FCSTD DOCUMENT  (FreeCAD 0.20R29177 (Git))
Label: Frame_Shape_T
License: All rights reserved
LicenseURL: http://en.wikipedia.org/wiki/All_rights_reserved
objects: App::Link×4, Spreadsheet::Sheet×1, App::Part×1
EXTERNAL_REF file=Frame_Bracket_End_OneHole.FCStd obj=PocketBody
EXTERNAL_REF file=Frame_Bracket_End_TwoHole.FCStd obj=PadBody
EXTERNAL_REF file=../../Master_of_Puppets.FCStd obj=Alternator
EXTERNAL_REF file=../../Master_of_Puppets.FCStd obj=Spreadsheet
EXTERNAL_REF file=../../Master_of_Puppets.FCStd obj=WindTurbine
EXTERNAL_REF file=../../YawBearing/YawBearing_Plate_Bottom.FCStd obj=PocketBody
EXTERNAL_REF file=Frame_Channel.FCStd obj=Body

FEATURE [App::Link] Link001  label="Bracket_End_OneHole"
  LinkPlacement = pos=(0,0,0) rot=(0,1,0;3.14159rad)
  LinkTransform = true
  LinkedObject = -> <external Frame_Bracket_End_OneHole.FCStd>#PocketBody
  Placement = pos=(0,0,0) rot=(0,1,0;3.14159rad)
FEATURE [App::Link] Link002  label="Bracket_End_TwoHole"
  LinkPlacement = pos=(0,0,237.25) rot=(0,1,0;3.14159rad)
  LinkTransform = true
  LinkedObject = -> <external Frame_Bracket_End_TwoHole.FCStd>#PadBody
  Placement = pos=(0,0,237.25) rot=(0,1,0;3.14159rad)
  expr: .LinkPlacement.Base.z = Spreadsheet.ChannelSectionHeight
FEATURE [Spreadsheet::Sheet] Spreadsheet
  cells = A1=Inputs; A2=ChannelSectionHeight; B2(ChannelSectionHeight)==Master_of_Puppets#Alternator.BC; A3=MetalLengthL; B3(MetalLengthL)==Master_of_Puppets#Spreadsheet.MetalLengthL; A4=MetalThicknessL; B4(MetalThicknessL)==Master_of_Puppets#Spreadsheet.MetalThicknessL; A5=SmallVerticalDistanceFromCenter; B5(SmallVerticalDistanceFromCenter)==Master_of_Puppets#WindTurbine.SmallVerticalDistanceFromCenter; A6=Calculated; A7=BottomPlateX; B7(BottomPlateX)==-SmallVerticalDistanceFromCenter; A8=BottomPlateY; B8(BottomPlateY)==MetalLengthL - MetalThicknessL; A9=BottomPlateZ; B9(BottomPlateZ)==ChannelSectionHeight + MetalThicknessL
FEATURE [App::Link] Link003  label="Plate_Bottom"
  LinkPlacement = pos=(-147.5,44,243.25) rot=(0.707107,0,0.707107;3.14159rad)
  LinkedObject = -> <external ../../YawBearing/YawBearing_Plate_Bottom.FCStd>#PocketBody
  Placement = pos=(-147.5,44,243.25) rot=(0.707107,0,0.707107;3.14159rad)
  expr: .Placement.Base.x = Spreadsheet.BottomPlateX
  expr: .Placement.Base.y = Spreadsheet.BottomPlateY
  expr: .Placement.Base.z = Spreadsheet.BottomPlateZ
FEATURE [App::Link] Link004  label="Channel"
  LinkTransform = true
  LinkedObject = -> <external Frame_Channel.FCStd>#Body
FEATURE [App::Part] Part  label="Frame_Shape_T"
  Group = -> [Link004,Link001,Link002,Link003]
  Origin = -> Origin

RESOLVED EXTERNAL PARTS (link-assembly join: the EXTERNAL_REF files above that resolve inside this repo's crawl, each included once):
---- part ../../Master_of_Puppets.FCStd = doc fcstd_6404554055c4 (61625 chars; too large to inline — full recipe in that document) ----
---- part ../../YawBearing/YawBearing_Plate_Bottom.FCStd = doc fcstd_9afb94730c02 ----
FCSTD DOCUMENT  (FreeCAD 0.21R33675 (Git))
Label: YawBearing_Plate_Bottom
License: All rights reserved
LicenseURL: http://en.wikipedia.org/wiki/All_rights_reserved
objects: Sketcher::SketchObject×2, PartDesign::Pad×1, PartDesign::Pocket×1, Spreadsheet::Sheet×1, PartDesign::Body×1
note: 7 computed .brp shape members not serialized (recipe doc carries the construction recipe); baked Part::Feature solids carry a one-line shape summary decoded from their .brp
EXTERNAL_REF file=../Master_of_Puppets.FCStd obj=Alternator
EXTERNAL_REF file=../Master_of_Puppets.FCStd obj=Spreadsheet
EXTERNAL_REF file=../Master_of_Puppets.FCStd obj=YawBearing

FEATURE [Sketcher::SketchObject] Sketch
  FullyConstrained = true
  MapMode = 5
  Support = -> [XY_Plane001]
  expr: Constraints[10] = Spreadsheet.Width
  expr: Constraints[9] = Spreadsheet.Length
  sketch-geometry (4):
    g0: LineSegment StartX=0 StartY=0 StartZ=0 EndX=48.25 EndY=0 EndZ=0
    g1: LineSegment StartX=48.25 StartY=0 StartZ=0 EndX=48.25 EndY=75.15 EndZ=0
    g2: LineSegment StartX=48.25 StartY=75.15 StartZ=0 EndX=0 EndY=75.15 EndZ=0
    g3: LineSegment StartX=0 StartY=75.15 StartZ=0 EndX=0 EndY=0 EndZ=0
  constraints (11):
    c: Coincident(g0,g1)
    c: Coincident(g1,g2)
    c: Coincident(g2,g3)
    c: Coincident(g3,g0)
    c: Horizontal(g0)
    c: Horizontal(g2)
    c: Vertical(g1)
    c: Vertical(g3)
    c: Coincident(g0,g-1)
    c: Distance(g3) = 75.15
    c: Distance(g2) = 48.25
FEATURE [PartDesign::Pad] Pad
  AllowMultiFace = false
  Direction = (0,0,1)
  Length = 10
  Length2 = 100
  Profile = -> Sketch
  Type = 0
  expr: Length = Spreadsheet.FlatMetalThickness
FEATURE [Sketcher::SketchObject] Sketch001
  ExternalGeometry = -> [Pad]
  FullyConstrained = true
  MapMode = 5
  Placement = pos=(0,0,10) rot=(0,0,1;0rad)
  Support = -> [Pad]
  expr: Constraints[0] = Spreadsheet.YawPipeRadius
  expr: Constraints[3] = Spreadsheet.YawBearingPlateCornerChamferLength
  sketch-geometry (4):
    g0: Circle CenterX=48.25 CenterY=75.15 CenterZ=0 NormalX=0 NormalY=0 NormalZ=1 AngleXU=0 Radius=30.15
    g1: LineSegment StartX=0 StartY=10 StartZ=0 EndX=10 EndY=0 EndZ=0
    g2: LineSegment StartX=0 StartY=10 StartZ=0 EndX=0 EndY=0 EndZ=0
    g3: LineSegment StartX=0 StartY=0 StartZ=0 EndX=10 EndY=0 EndZ=0
  constraints (10):
    c: Radius(g0) = 30.15
    c: PointOnObject(g1,g-6)
    c: PointOnObject(g1,g-5)
    c: DistanceY(g-1,g1) = 10
    c: Coincident(g2,g1)
    c: Coincident(g2,g-1)
    c: Coincident(g3,g-1)
    c: Coincident(g3,g1)
    c: Coincident(g-4,g0)
    c: Equal(g3,g2)
FEATURE [PartDesign::Pocket] Pocket
  AllowMultiFace = false
  BaseFeature = -> Pad
  Direction = (0,0,-1)
  Length = 5
  Length2 = 100
  Profile = -> Sketch001
  Type = 1
FEATURE [Spreadsheet::Sheet] Spreadsheet
  cells = A1='Inputs; A2='YawPipeDiameter; B2(YawPipeDiameter)==Master_of_Puppets#Spreadsheet.YawPipeDiameter; A3='FlatMetalThickness; B3(FlatMetalThickness)==Master_of_Puppets#Spreadsheet.FlatMetalThickness; A4='I; B4(I)==Master_of_Puppets#Alternator.I; A5='j; B5(j)==Master_of_Puppets#Alternator.j; A6='YawBearingPlateCornerChamferLength; B6(YawBearingPlateCornerChamferLength)==Master_of_Puppets#YawBearing.YawBearingPlateCornerChamferLength; A7='Calculated; A8='YawPipeRadius; B8(YawPipeRadius)==YawPipeDiameter / 2; A9='Length; B9(Length)==YawPipeRadius + j; A10='Width; B10(Width)==YawPipeRadius + I
FEATURE [PartDesign::Body] PocketBody  label="YawBearing_Plate_Bottom"
  Group = -> [Sketch,Pad,Sketch001,Pocket]
  Openafpm_Flat = true
  Origin = -> Origin001
  Tip = -> Pocket
---- part Frame_Bracket_End_OneHole.FCStd = doc fcstd_23a8c28440bc ----
FCSTD DOCUMENT  (FreeCAD 0.20R29177 (Git))
Label: Frame_Bracket_End_OneHole
License: All rights reserved
LicenseURL: http://en.wikipedia.org/wiki/All_rights_reserved
objects: Sketcher::SketchObject×2, PartDesign::Pad×1, Spreadsheet::Sheet×1, PartDesign::Pocket×1, PartDesign::Body×1
note: 7 computed .brp shape members not serialized (recipe doc carries the construction recipe); baked Part::Feature solids carry a one-line shape summary decoded from their .brp
EXTERNAL_REF file=../../Master_of_Puppets.FCStd obj=Alternator
EXTERNAL_REF file=../../Master_of_Puppets.FCStd obj=Spreadsheet

FEATURE [Sketcher::SketchObject] Sketch
  FullyConstrained = true
  MapMode = 5
  Support = -> [XY_Plane001]
  expr: Constraints[14] = Spreadsheet.Length
  expr: Constraints[15] = Spreadsheet.Thickness
  sketch-geometry (6):
    g0: LineSegment StartX=0 StartY=0 StartZ=0 EndX=0 EndY=50 EndZ=0
    g1: LineSegment StartX=0 StartY=50 StartZ=0 EndX=6 EndY=50 EndZ=0
    g2: LineSegment StartX=6 StartY=50 StartZ=0 EndX=6 EndY=6 EndZ=0
    g3: LineSegment StartX=6 StartY=6 StartZ=0 EndX=50 EndY=6 EndZ=0
    g4: LineSegment StartX=50 StartY=6 StartZ=0 EndX=50 EndY=0 EndZ=0
    g5: LineSegment StartX=50 StartY=0 StartZ=0 EndX=0 EndY=0 EndZ=0
  constraints (17):
    c: Coincident(g-1,g0)
    c: Vertical(g0)
    c: Coincident(g0,g1)
    c: Horizontal(g1)
    c: Coincident(g1,g2)
    c: Vertical(g2)
    c: Coincident(g2,g3)
    c: Horizontal(g3)
    c: Coincident(g3,g4)
    c: PointOnObject(g4,g-1)
    c: Vertical(g4)
    c: Coincident(g4,g5)
    c: Equal(g1,g4)
    c: Equal(g0,g5)
    c: DistanceY(g0,g0) = 50
    c: DistanceX(g1,g1) = 6
    c: Coincident(g5,g-1)
FEATURE [PartDesign::Pad] Pad
  AllowMultiFace = false
  Direction = (0,0,1)
  Length = 100
  Length2 = 100
  Profile = -> Sketch
  Type = 0
  expr: Length = Spreadsheet.Depth
FEATURE [Spreadsheet::Sheet] Spreadsheet
  cells = A1=Inputs; A2=Thickness; B2(Thickness)==Master_of_Puppets#Spreadsheet.MetalThicknessL; A3=Length; B3(Length)==Master_of_Puppets#Spreadsheet.MetalLengthL; A4=HolesRadius; B4(HolesRadius)==Master_of_Puppets#Alternator.HolesRadius; A5=Depth; B5(Depth)==Master_of_Puppets#Alternator.D; A6=Calculated; A7=CircleXCenter; B7(CircleXCenter)==Length / 2; A8=CircleYCenter; B8(CircleYCenter)==Depth / 2
FEATURE [Sketcher::SketchObject] Sketch001
  FullyConstrained = true
  MapMode = 5
  Placement = pos=(0,0,0) rot=(1,0,0;1.5708rad)
  Support = -> [Pad]
  expr: Constraints[2] = Spreadsheet.CircleYCenter
  expr: Constraints[3] = Spreadsheet.HolesRadius
  expr: Constraints[5] = Spreadsheet.CircleXCenter
  sketch-geometry (2):
    g0: LineSegment StartX=0 StartY=0 StartZ=0 EndX=0 EndY=50 EndZ=0
    g1: Circle CenterX=25 CenterY=50 CenterZ=0 NormalX=0 NormalY=0 NormalZ=1 AngleXU=0 Radius=6
  constraints (6):
    c: Coincident(g0,g-1)
    c: PointOnObject(g0,g-2)
    c: DistanceY(g0,g0) = 50
    c: Radius(g1) = 6
    c: Horizontal(g1,g0)
    c: DistanceX(g-2,g1) = 25
FEATURE [PartDesign::Pocket] Pocket
  AllowMultiFace = false
  BaseFeature = -> Pad
  Direction = (0,1,-2e-16)
  Length = 5
  Length2 = 100
  Profile = -> Sketch001
  Type = 1
FEATURE [PartDesign::Body] PocketBody  label="Frame_Bracket_End_OneHole"
  Group = -> [Sketch,Pad,Sketch001,Pocket]
  Origin = -> Origin001
  Placement = pos=(-50,50,0) rot=(0.707107,0,0.707107;3.14159rad)
  Tip = -> Pocket
  expr: .Placement.Base.x = -<<Spreadsheet>>.Depth / 2
  expr: .Placement.Base.y = <<Spreadsheet>>.Length
---- part Frame_Bracket_End_TwoHole.FCStd = doc fcstd_d64d4ceb8c3d ----
FCSTD DOCUMENT  (FreeCAD 0.20R29177 (Git))
Label: Frame_Bracket_End_TwoHole
License: All rights reserved
LicenseURL: http://en.wikipedia.org/wiki/All_rights_reserved
objects: Sketcher::SketchObject×2, PartDesign::Pad×1, Spreadsheet::Sheet×1, PartDesign::Pocket×1, PartDesign::Body×1
note: 7 computed .brp shape members not serialized (recipe doc carries the construction recipe); baked Part::Feature solids carry a one-line shape summary decoded from their .brp
EXTERNAL_REF file=../../Master_of_Puppets.FCStd obj=Alternator
EXTERNAL_REF file=../../Master_of_Puppets.FCStd obj=Spreadsheet

FEATURE [Sketcher::SketchObject] Sketch
  FullyConstrained = true
  MapMode = 5
  Support = -> [XY_Plane001]
  expr: Constraints[14] = Spreadsheet.MetalLengthL
  expr: Constraints[15] = Spreadsheet.MetalThicknessL
  sketch-geometry (6):
    g0: LineSegment StartX=0 StartY=0 StartZ=0 EndX=0 EndY=50 EndZ=0
    g1: LineSegment StartX=0 StartY=50 StartZ=0 EndX=6 EndY=50 EndZ=0
    g2: LineSegment StartX=6 StartY=50 StartZ=0 EndX=6 EndY=6 EndZ=0
    g3: LineSegment StartX=6 StartY=6 StartZ=0 EndX=50 EndY=6 EndZ=0
    g4: LineSegment StartX=50 StartY=6 StartZ=0 EndX=50 EndY=0 EndZ=0
    g5: LineSegment StartX=50 StartY=0 StartZ=0 EndX=0 EndY=0 EndZ=0
  constraints (17):
    c: Coincident(g-1,g0)
    c: Vertical(g0)
    c: Coincident(g0,g1)
    c: Horizontal(g1)
    c: Coincident(g1,g2)
    c: Vertical(g2)
    c: Coincident(g2,g3)
    c: Horizontal(g3)
    c: Coincident(g3,g4)
    c: PointOnObject(g4,g-1)
    c: Vertical(g4)
    c: Coincident(g4,g5)
    c: Equal(g1,g4)
    c: Equal(g0,g5)
    c: DistanceY(g0,g0) = 50
    c: DistanceX(g1,g1) = 6
    c: Coincident(g5,g-1)
FEATURE [PartDesign::Pad] Pad
  AllowMultiFace = false
  Direction = (0,0,1)
  Length = 381.688
  Length2 = 100
  Profile = -> Sketch
  Type = 0
  expr: Length = Spreadsheet.Length
FEATURE [Spreadsheet::Sheet] Spreadsheet
  cells = A1=Inputs; A2=RotorDiskRadius; B2(RotorDiskRadius)==Master_of_Puppets#Spreadsheet.RotorDiskRadius; A3='CalculatedWindTurbineShape; B3(CalculatedWindTurbineShape)==Master_of_Puppets#Spreadsheet.CalculatedWindTurbineShape; A4=MetalThicknessL; B4(MetalThicknessL)==Master_of_Puppets#Spreadsheet.MetalThicknessL; A5=MetalLengthL; B5(MetalLengthL)==Master_of_Puppets#Spreadsheet.MetalLengthL; A6=HolesRadius; B6(HolesRadius)==Master_of_Puppets#Alternator.HolesRadius; A7=DistanceBetweenCenterOfHoleAndFrameEdge; B7(DistanceBetweenCenterOfHoleAndFrameEdge)==Master_of_Puppets#Alternator.DistanceBetweenCenterOfHoleAndFrameEdge; A8=Length; A9=TShapeLength; B9(TShapeLength)==Master_of_Puppets#Alternator.TShapeTwoHoleEndBracketLength; A10=HShapeLength; B10(HShapeLength)==Master_of_Puppets#Alternator.GG; A11=StarShapeLength; B11(StarShapeLength)==Master_of_Puppets#Alternator.StarShapeTwoHoleEndBracketLength; A12=Length; B12(Length)==CalculatedWindTurbineShape == <<T>> ? TShapeLength : (CalculatedWindTurbineShape == <<H>> ? HShapeLength : StarShapeLength)
FEATURE [Sketcher::SketchObject] CopySketch001  label="Pocket001"
  FullyConstrained = true
  Placement = pos=(0,0,0) rot=(1,0,0;1.5708rad)
  Support = -> [Pad]
  expr: Constraints[0] = Spreadsheet.HolesRadius
  expr: Constraints[1] = Spreadsheet.DistanceBetweenCenterOfHoleAndFrameEdge
  expr: Constraints[2] = Spreadsheet.DistanceBetweenCenterOfHoleAndFrameEdge
  expr: Constraints[3] = Spreadsheet.DistanceBetweenCenterOfHoleAndFrameEdge
  expr: Constraints[4] = Spreadsheet.Length - Spreadsheet.DistanceBetweenCenterOfHoleAndFrameEdge
  sketch-geometry (2):
    g0: Circle CenterX=25 CenterY=25 CenterZ=0 NormalX=0 NormalY=0 NormalZ=1 AngleXU=0 Radius=6
    g1: Circle CenterX=25 CenterY=356.688 CenterZ=0 NormalX=0 NormalY=0 NormalZ=1 AngleXU=0 Radius=6
  constraints (6):
    c: Radius(g0) = 6
    c: DistanceX(g-2,g0) = 25
    c: DistanceY(g-1,g0) = 25
    c: DistanceX(g-2,g1) = 25
    c: DistanceY(g-1,g1) = 356.688
    c: Equal(g1,g0)
FEATURE [PartDesign::Pocket] Pocket
  AllowMultiFace = false
  BaseFeature = -> Pad
  Direction = (0,1,-2e-16)
  Length = 5
  Length2 = 100
  Profile = -> CopySketch001
  Type = 1
FEATURE [PartDesign::Body] PadBody  label="Frame_Bracket_End_TwoHole"
  Group = -> [Sketch,Pad,Pocket]
  Origin = -> Origin001
  Placement = pos=(190.844,50,0) rot=(0.707107,0,-0.707107;3.14159rad)
  Tip = -> Pocket
  expr: .Placement.Base.x = Spreadsheet.Length / 2
  expr: .Placement.Base.y = Spreadsheet.MetalLengthL
---- part Frame_Channel.FCStd = doc fcstd_9cdf3fa85351 ----
FCSTD DOCUMENT  (FreeCAD 1.0R39109 (Git))
Label: Frame_Channel
License: All rights reserved
LicenseURL: http://en.wikipedia.org/wiki/All_rights_reserved
objects: Sketcher::SketchObject×2, PartDesign::Pad×1, Spreadsheet::Sheet×1, PartDesign::Mirrored×1, PartDesign::Pocket×1, PartDesign::Body×1
note: 13 computed .brp shape members not serialized (recipe doc carries the construction recipe); baked Part::Feature solids carry a one-line shape summary decoded from their .brp
EXTERNAL_REF file=../../Master_of_Puppets.FCStd obj=Alternator
EXTERNAL_REF file=../../Master_of_Puppets.FCStd obj=Hub
EXTERNAL_REF file=../../Master_of_Puppets.FCStd obj=Spreadsheet

FEATURE [Sketcher::SketchObject] Sketch
  ArcFitTolerance = 0
  AttachmentSupport = -> [XY_Plane]
  FullyConstrained = true
  MakeInternals = false
  MapMode = 5
  expr: Constraints[11] = Spreadsheet.MetalLengthL
  expr: Constraints[12] = Spreadsheet.MetalLengthL
  expr: Constraints[13] = Spreadsheet.MetalThicknessL
  expr: Constraints[15] = Spreadsheet.MetalThicknessL
  sketch-geometry (6):
    g0: LineSegment StartX=0 StartY=50 StartZ=0 EndX=0 EndY=0 EndZ=0
    g1: LineSegment StartX=0 StartY=0 StartZ=0 EndX=50 EndY=0 EndZ=0
    g2: LineSegment StartX=50 StartY=0 StartZ=0 EndX=50 EndY=6 EndZ=0
    g3: LineSegment StartX=50 StartY=6 StartZ=0 EndX=6 EndY=6 EndZ=0
    g4: LineSegment StartX=6 StartY=6 StartZ=0 EndX=6 EndY=50 EndZ=0
    g5: LineSegment StartX=6 StartY=50 StartZ=0 EndX=0 EndY=50 EndZ=0
  constraints (17):
    c: Vertical(g0)
    c: Coincident(g0,g1)
    c: Horizontal(g1)
    c: Coincident(g1,g2)
    c: Vertical(g2)
    c: Coincident(g2,g3)
    c: Horizontal(g3)
    c: Coincident(g3,g4)
    c: Vertical(g4)
    c: Coincident(g4,g5)
    c: Coincident(g5,g0)
    c: DistanceX(g1,g1) = 50
    c: DistanceY(g0,g0) = 50
    c: DistanceY(g2,g2) = 6
    c: Horizontal(g5)
    c: DistanceX(g5,g5) = 6
    c: Coincident(g0,g-1)
FEATURE [PartDesign::Pad] Pad
  AllowMultiFace = false
  Direction = (0,0,1)
  Length = 238.75
  Length2 = 100
  Profile = -> Sketch
  Suppressed = false
  Type = 0
  expr: Length = Spreadsheet.Depth
FEATURE [Spreadsheet::Sheet] Spreadsheet
  cells = A1='Inputs; A2='MetalLengthL; B2(MetalLengthL)==Master_of_Puppets#Spreadsheet.MetalLengthL; A3='MetalThicknessL; B3(MetalThicknessL)==Master_of_Puppets#Spreadsheet.MetalThicknessL; A4='CalculatedWindTurbineShape; B4(CalculatedWindTurbineShape)==Master_of_Puppets#Spreadsheet.CalculatedWindTurbineShape; A5='StubAxleShaftRadius; B5(StubAxleShaftRadius)==Master_of_Puppets#Hub.StubAxleShaftRadius; A6='CoilLegWidth; B6(CoilLegWidth)==Master_of_Puppets#Spreadsheet.CoilLegWidth; A7='Depth; A8='TShapeLength; B8(TShapeLength)==Master_of_Puppets#Alternator.BC; A9='HShapeLength; B9(HShapeLength)==Master_of_Puppets#Alternator.HH; A10='StarShapeLength; B10(StarShapeLength)==Master_of_Puppets#Alternator.B; A11='Depth; B11(Depth)==CalculatedWindTurbineShape == <<T>> ? TShapeLength : (CalculatedWindTurbineShape == <<H>> ? HShapeLength : StarShapeLength); A12='HoleDistance; A13='OffsetHole; B13(OffsetHole)==Master_of_Puppets#Alternator.X; A14='MidpointHole; B14(MidpointHole)==Depth / 2; A15='HoleDistance; B15(HoleDistance)==CalculatedWindTurbineShape == <<T>> ? OffsetHole : MidpointHole; A16='Channel; A17='X; B17='Y; C17='Z; A18(ChannelX)==-MetalLengthL; B18(ChannelY)=0; C18(ChannelZ)==Depth
FEATURE [Sketcher::SketchObject] Sketch001
  ArcFitTolerance = 0
  AttachmentSupport = -> [Pad]
  FullyConstrained = true
  MakeInternals = false
  MapMode = 5
  Placement = pos=(6,0,0) rot=(0.57735,0.57735,0.57735;2.0944rad)
  expr: Constraints[0] = Spreadsheet.StubAxleShaftRadius
  expr: Constraints[1] = Spreadsheet.MetalLengthL
  expr: Constraints[2] = Spreadsheet.HoleDistance
  sketch-geometry (1):
    g0: Circle CenterX=50 CenterY=71.25 CenterZ=0 NormalX=0 NormalY=0 NormalZ=1 AngleXU=0 Radius=18
  constraints (3):
    c: Radius(g0) = 18
    c: Distance(g0,g-2) = 50
    c: Distance(g0,g-1) = 71.25
FEATURE [PartDesign::Mirrored] Mirrored
  BaseFeature = -> Pad
  MirrorPlane = -> Pad [Face6]
  Originals = -> [Pad]
  Suppressed = false
  TransformMode = 0
FEATURE [PartDesign::Pocket] Pocket
  BaseFeature = -> Mirrored
  Direction = (-1,0,0)
  Length = 6
  Length2 = 100
  Profile = -> Sketch001
  Suppressed = false
  Type = 0
  expr: Length = Spreadsheet.MetalThicknessL
FEATURE [PartDesign::Body] Body  label="Frame_Channel"
  AllowCompound = false
  Group = -> [Sketch,Pad,Sketch001,Mirrored,Pocket]
  Origin = -> Origin
  Placement = pos=(-50,0,238.75) rot=(0.707107,0.707107,0;3.14159rad)
  Tip = -> Pocket
  expr: .Placement.Base.x = Spreadsheet.ChannelX
  expr: .Placement.Base.y = Spreadsheet.ChannelY
  expr: .Placement.Base.z = Spreadsheet.ChannelZ
